annotation { "Feature Type Name" : "Feature", "Feature Type Description" : "" }
export const myFeature = defineFeature(function(context is Context, id is Id, definition is map)
    precondition{}
    {
        {
            var Q0;
            Q0=qCreatedBy(makeId("Front.planeOp"),FACE);
            var sketch = newSketch(context, id + "F0", { "sketchPlane" : qUnion([Q0])});
            skLineSegment(sketch, "E0", {"start": v(0, 22.3) * mm, "end": v(0, 0) * mm, "construction": true});
            skFitSpline(sketch, "E1", {"points": [v(-61.07, -6.98) * mm, v(-58.94, -7.84) * mm, v(-56.34, -8.22) * mm, v(-48.16, -8.6) * mm, v(-38.05, -8.76) * mm, v(-26.12, -8.98) * mm, v(-21.91, -9.15) * mm, v(-14.6, -9.33) * mm, v(-3.24, -9.5) * mm, v(13.49, -9.38) * mm, v(17.24, -9.26) * mm, v(19, -9.14) * mm, v(20.21, -8.9) * mm, v(21.52, -8.48) * mm, v(22.05, -7.83) * mm, v(22.5, -7.27) * mm, v(23.16, -6.84) * mm, v(23.97, -6.5) * mm, v(24.57, -5.86) * mm, v(24.95, -5.03) * mm, v(24.92, -4.13) * mm, v(24.43, -3.44) * mm, v(23.83, -2.92) * mm, v(23.16, -2.63) * mm, v(22.5, -2.17) * mm, v(22.12, -2.03) * mm, v(21.75, -1.57) * mm, v(21.09, -1.13) * mm, v(20.4, -0.79) * mm, v(19.33, -0.56) * mm, v(17.83, -0.36) * mm, v(16.39, -0.24) * mm, v(14.53, -0.14) * mm, v(12.17, -0.05) * mm, v(10.07, 0) * mm], "startDerivative": vector(72.66, -33.25) * mm, "endDerivative": vector(-73.02, 1.43) * mm});
            skArc(sketch, "E2", {"start": v(18.34, 2.78) * mm, "mid": v(14.1, 1.7) * mm, "end": v(10.07, 0) * mm});
            skLineSegment(sketch, "E3", {"start": v(-61.07, -6.98) * mm, "end": v(-61.07, -2.65) * mm});
            skArc(sketch, "E4", {"start": v(18.34, 2.78) * mm, "mid": v(20.82, 2.08) * mm, "end": v(23.39, 1.8) * mm});
            skArc(sketch, "E5", {"start": v(23.39, 1.8) * mm, "mid": v(26.49, 1.03) * mm, "end": v(29.58, 1.8) * mm});
            skArc(sketch, "E6", {"start": v(29.58, 1.8) * mm, "mid": v(32.23, 2.03) * mm, "end": v(34.77, 2.78) * mm});
            skLineSegment(sketch, "E7", {"start": v(34.77, 2.78) * mm, "end": v(61.14, 3.32) * mm});
            skLineSegment(sketch, "E8", {"start": v(61.14, 3.32) * mm, "end": v(62.06, 5.86) * mm});
            skLineSegment(sketch, "E9", {"start": v(62.06, 5.86) * mm, "end": v(47.49, 5.86) * mm});
            skLineSegment(sketch, "E10", {"start": v(47.49, 5.86) * mm, "end": v(47.03, 6.17) * mm});
            skLineSegment(sketch, "E11", {"start": v(47.03, 6.17) * mm, "end": v(43.68, 6.17) * mm});
            skArc(sketch, "E12", {"start": v(35.62, 7.65) * mm, "mid": v(39.58, 6.54) * mm, "end": v(43.68, 6.17) * mm});
            skLineSegment(sketch, "E13", {"start": v(35.62, 7.65) * mm, "end": v(34.47, 8.77) * mm});
            skLineSegment(sketch, "E14", {"start": v(34.47, 8.77) * mm, "end": v(30.37, 8.77) * mm});
            skLineSegment(sketch, "E15", {"start": v(30.37, 8.77) * mm, "end": v(29.74, 9.25) * mm});
            skLineSegment(sketch, "E16", {"start": v(29.74, 9.25) * mm, "end": v(29.74, 9.51) * mm});
            skArc(sketch, "E17", {"start": v(29.74, 9.51) * mm, "mid": v(29.04, 9.84) * mm, "end": v(28.29, 9.97) * mm});
            skLineSegment(sketch, "E18", {"start": v(28.29, 9.97) * mm, "end": v(27.74, 9.97) * mm});
            skArc(sketch, "E19", {"start": v(27.74, 9.97) * mm, "mid": v(26.66, 10.33) * mm, "end": v(25.58, 9.97) * mm});
            skLineSegment(sketch, "E20", {"start": v(25.58, 9.97) * mm, "end": v(22.22, 9.85) * mm});
            skArc(sketch, "E21", {"start": v(22.22, 9.85) * mm, "mid": v(21.65, 9.7) * mm, "end": v(21.2, 9.32) * mm});
            skLineSegment(sketch, "E22", {"start": v(21.2, 9.32) * mm, "end": v(0.14, 10) * mm});
            skLineSegment(sketch, "E23", {"start": v(0.14, 10) * mm, "end": v(-2.32, 11.15) * mm});
            skPoint(sketch, "E23.endSnap0", {"position": v(0, 11.15) * mm});
            skArc(sketch, "E24", {"start": v(-2.32, 11.15) * mm, "mid": v(-0.13, 11.24) * mm, "end": v(2.04, 11.57) * mm});
            skArc(sketch, "E25", {"start": v(2.04, 11.57) * mm, "mid": v(3, 11.9) * mm, "end": v(3.7, 12.63) * mm});
            skLineSegment(sketch, "E26", {"start": v(3.7, 12.63) * mm, "end": v(3.7, 13.61) * mm});
            skLineSegment(sketch, "E27", {"start": v(3.7, 13.61) * mm, "end": v(5.25, 13.61) * mm});
            skArc(sketch, "E28", {"start": v(5.25, 13.61) * mm, "mid": v(5.55, 12.74) * mm, "end": v(6.1, 12.02) * mm});
            skLineSegment(sketch, "E29", {"start": v(6.1, 12.02) * mm, "end": v(6.52, 12.02) * mm});
            skLineSegment(sketch, "E30", {"start": v(6.52, 12.02) * mm, "end": v(6.52, 18.6) * mm});
            skLineSegment(sketch, "E31", {"start": v(6.52, 18.6) * mm, "end": v(6.1, 18.6) * mm});
            skArc(sketch, "E32", {"start": v(6.1, 18.6) * mm, "mid": v(5.55, 17.74) * mm, "end": v(5.25, 16.77) * mm});
            skLineSegment(sketch, "E33", {"start": v(5.25, 16.77) * mm, "end": v(3.79, 16.77) * mm});
            skLineSegment(sketch, "E34", {"start": v(3.79, 16.77) * mm, "end": v(3.79, 17.93) * mm});
            skArc(sketch, "E35", {"start": v(3.79, 17.93) * mm, "mid": v(2.94, 18.66) * mm, "end": v(1.86, 18.94) * mm});
            skLineSegment(sketch, "E36", {"start": v(1.86, 18.94) * mm, "end": v(-0.16, 19.06) * mm});
            skArc(sketch, "E37", {"start": v(-0.16, 19.06) * mm, "mid": v(-0.64, 19.4) * mm, "end": v(-1.22, 19.53) * mm});
            skFitSpline(sketch, "E38", {"points": [v(-1.22, 19.53) * mm, v(-2.68, 19.64) * mm, v(-5.39, 19.67) * mm, v(-7.1, 19.65) * mm, v(-13.35, 19.67) * mm, v(-26.7, 19.24) * mm, v(-37.9, 18.34) * mm], "startDerivative": vector(-14.6, 1.5) * mm, "endDerivative": vector(-43.75, -4.05) * mm});
            skFitSpline(sketch, "E39", {"points": [v(-37.9, 18.34) * mm, v(-38.41, 17.33) * mm, v(-39.6, 16.45) * mm, v(-41.1, 15.84) * mm, v(-42.02, 15.63) * mm], "startDerivative": vector(-1.75, -4.5) * mm, "endDerivative": vector(-4, -0.72) * mm});
            skLineSegment(sketch, "E40", {"start": v(-42.02, 15.63) * mm, "end": v(-42.02, 13.4) * mm});
            skFitSpline(sketch, "E41", {"points": [v(-42.02, 13.4) * mm, v(-39.98, 13.28) * mm, v(-37.97, 13.08) * mm, v(-36.61, 12.92) * mm], "startDerivative": vector(5.67, -0.24) * mm, "endDerivative": vector(4.42, -0.52) * mm});
            skFitSpline(sketch, "E42", {"points": [v(-36.61, 12.92) * mm, v(-36.14, 12.41) * mm, v(-35.35, 11.98) * mm], "startDerivative": vector(0.9, -1.15) * mm, "endDerivative": vector(1.6, -0.75) * mm});
            skFitSpline(sketch, "E43", {"points": [v(-35.35, 11.98) * mm, v(-30.42, 11.58) * mm, v(-24.46, 11.34) * mm, v(-19.95, 11.19) * mm, v(-17.23, 11.19) * mm], "startDerivative": vector(18.11, -1.69) * mm, "endDerivative": vector(13.15, 0.13) * mm});
            skLineSegment(sketch, "E44", {"start": v(-17.23, 11.19) * mm, "end": v(-10.45, 8.48) * mm});
            skLineSegment(sketch, "E45", {"start": v(-10.45, 8.48) * mm, "end": v(-8.63, 6.53) * mm});
            skLineSegment(sketch, "E46", {"start": v(-8.63, 6.53) * mm, "end": v(-10.68, 5.14) * mm});
            skLineSegment(sketch, "E47", {"start": v(-10.68, 5.14) * mm, "end": v(-8.18, 3.37) * mm});
            skLineSegment(sketch, "E48", {"start": v(-8.18, 3.37) * mm, "end": v(-4.86, 3.37) * mm});
            skLineSegment(sketch, "E49", {"start": v(-4.86, 3.37) * mm, "end": v(-5.27, 2.44) * mm});
            skLineSegment(sketch, "E50", {"start": v(-5.27, 2.44) * mm, "end": v(-13.89, 0) * mm});
            skFitSpline(sketch, "E51", {"points": [v(-61.07, -2.65) * mm, v(-60.98, -2.39) * mm, v(-60.7, -2.23) * mm, v(-59.8, -2.03) * mm, v(-58.51, -1.75) * mm, v(-57.1, -1.48) * mm, v(-56.48, -1.4) * mm, v(-55.65, -1.24) * mm, v(-46.62, -0.9) * mm, v(-37.29, -0.61) * mm, v(-28, -0.37) * mm, v(-13.89, 0) * mm], "startDerivative": vector(1.99, 10.5) * mm, "endDerivative": vector(74.9, 2) * mm});
            skSolve(sketch);
        }
        {
            var Q0;
            Q0 = qSketchRegion(id + "F0", true);
            extrude(context, id + "F1", {"entities" : qUnion([Q0]), "depth" : 2 * mm, "offsetDistance" : 25 * mm});
        }
        {
            var Q0;
            Q0=makeQuery(id+"F1.opExtrude","SWEPT_BODY",BODY,{"disambiguationData":[OSD([sQuery(id+"F0.wireOp",EDGE,"E1"),sQuery(id+"F0.wireOp",EDGE,"E2"),sQuery(id+"F0.wireOp",EDGE,"E3"),sQuery(id+"F0.wireOp",EDGE,"E4"),sQuery(id+"F0.wireOp",EDGE,"E5"),sQuery(id+"F0.wireOp",EDGE,"E6"),sQuery(id+"F0.wireOp",EDGE,"E7"),sQuery(id+"F0.wireOp",EDGE,"E8"),sQuery(id+"F0.wireOp",EDGE,"E9"),sQuery(id+"F0.wireOp",EDGE,"E10"),sQuery(id+"F0.wireOp",EDGE,"E11"),sQuery(id+"F0.wireOp",EDGE,"E12"),sQuery(id+"F0.wireOp",EDGE,"E13"),sQuery(id+"F0.wireOp",EDGE,"E14"),sQuery(id+"F0.wireOp",EDGE,"E15"),sQuery(id+"F0.wireOp",EDGE,"E16"),sQuery(id+"F0.wireOp",EDGE,"E17"),sQuery(id+"F0.wireOp",EDGE,"E18"),sQuery(id+"F0.wireOp",EDGE,"E19"),sQuery(id+"F0.wireOp",EDGE,"E20"),sQuery(id+"F0.wireOp",EDGE,"E21"),sQuery(id+"F0.wireOp",EDGE,"E22"),sQuery(id+"F0.wireOp",EDGE,"E23"),sQuery(id+"F0.wireOp",EDGE,"E24"),sQuery(id+"F0.wireOp",EDGE,"E25"),sQuery(id+"F0.wireOp",EDGE,"E26"),sQuery(id+"F0.wireOp",EDGE,"E27"),sQuery(id+"F0.wireOp",EDGE,"E28"),sQuery(id+"F0.wireOp",EDGE,"E29"),sQuery(id+"F0.wireOp",EDGE,"E30"),sQuery(id+"F0.wireOp",EDGE,"E31"),sQuery(id+"F0.wireOp",EDGE,"E32"),sQuery(id+"F0.wireOp",EDGE,"E33"),sQuery(id+"F0.wireOp",EDGE,"E34"),sQuery(id+"F0.wireOp",EDGE,"E35"),sQuery(id+"F0.wireOp",EDGE,"E36"),sQuery(id+"F0.wireOp",EDGE,"E37"),sQuery(id+"F0.wireOp",EDGE,"E38"),sQuery(id+"F0.wireOp",EDGE,"E39"),sQuery(id+"F0.wireOp",EDGE,"E40"),sQuery(id+"F0.wireOp",EDGE,"E41"),sQuery(id+"F0.wireOp",EDGE,"E42"),sQuery(id+"F0.wireOp",EDGE,"E43"),sQuery(id+"F0.wireOp",EDGE,"E44"),sQuery(id+"F0.wireOp",EDGE,"E45"),sQuery(id+"F0.wireOp",EDGE,"E46"),sQuery(id+"F0.wireOp",EDGE,"E47"),sQuery(id+"F0.wireOp",EDGE,"E48"),sQuery(id+"F0.wireOp",EDGE,"E49"),sQuery(id+"F0.wireOp",EDGE,"E50"),sQuery(id+"F0.wireOp",EDGE,"E51")])]});
            var Q1;
            Q1=makeQuery(id+"F1.opExtrude","CAP_EDGE",EDGE,{"disambiguationData":[OSD([sQuery(id+"F0.wireOp",EDGE,"E3")])],"isStart":false});
            var Q2;
            Q2=makeQuery(id+"F1.opExtrude","CAP_VERTEX",VERTEX,{"disambiguationData":[OSD([sQuery(id+"F0.wireOp",EDGE,"E1"),sQuery(id+"F0.wireOp",EDGE,"E3")])],"isStart":false});
            transform(context, id + "F2", {"entities" : qUnion([Q0]), "transformType" : TransformType.SCALE_UNIFORMLY, "scale" : 1.22, "scalePoint" : qUnion([Q2]), "makeCopy" : false});
        }
        {
            var Q0;
            Q0=makeQuery(id+"F1.opExtrude","CAP_FACE",FACE,{"disambiguationData":[OSD([sQuery(id+"F0.wireOp",EDGE,"E1"),sQuery(id+"F0.wireOp",EDGE,"E2"),sQuery(id+"F0.wireOp",EDGE,"E3"),sQuery(id+"F0.wireOp",EDGE,"E4"),sQuery(id+"F0.wireOp",EDGE,"E5"),sQuery(id+"F0.wireOp",EDGE,"E6"),sQuery(id+"F0.wireOp",EDGE,"E7"),sQuery(id+"F0.wireOp",EDGE,"E8"),sQuery(id+"F0.wireOp",EDGE,"E9"),sQuery(id+"F0.wireOp",EDGE,"E10"),sQuery(id+"F0.wireOp",EDGE,"E11"),sQuery(id+"F0.wireOp",EDGE,"E12"),sQuery(id+"F0.wireOp",EDGE,"E13"),sQuery(id+"F0.wireOp",EDGE,"E14"),sQuery(id+"F0.wireOp",EDGE,"E15"),sQuery(id+"F0.wireOp",EDGE,"E16"),sQuery(id+"F0.wireOp",EDGE,"E17"),sQuery(id+"F0.wireOp",EDGE,"E18"),sQuery(id+"F0.wireOp",EDGE,"E19"),sQuery(id+"F0.wireOp",EDGE,"E20"),sQuery(id+"F0.wireOp",EDGE,"E21"),sQuery(id+"F0.wireOp",EDGE,"E22"),sQuery(id+"F0.wireOp",EDGE,"E23"),sQuery(id+"F0.wireOp",EDGE,"E24"),sQuery(id+"F0.wireOp",EDGE,"E25"),sQuery(id+"F0.wireOp",EDGE,"E26"),sQuery(id+"F0.wireOp",EDGE,"E27"),sQuery(id+"F0.wireOp",EDGE,"E28"),sQuery(id+"F0.wireOp",EDGE,"E29"),sQuery(id+"F0.wireOp",EDGE,"E30"),sQuery(id+"F0.wireOp",EDGE,"E31"),sQuery(id+"F0.wireOp",EDGE,"E32"),sQuery(id+"F0.wireOp",EDGE,"E33"),sQuery(id+"F0.wireOp",EDGE,"E34"),sQuery(id+"F0.wireOp",EDGE,"E35"),sQuery(id+"F0.wireOp",EDGE,"E36"),sQuery(id+"F0.wireOp",EDGE,"E37"),sQuery(id+"F0.wireOp",EDGE,"E38"),sQuery(id+"F0.wireOp",EDGE,"E39"),sQuery(id+"F0.wireOp",EDGE,"E40"),sQuery(id+"F0.wireOp",EDGE,"E41"),sQuery(id+"F0.wireOp",EDGE,"E42"),sQuery(id+"F0.wireOp",EDGE,"E43"),sQuery(id+"F0.wireOp",EDGE,"E44"),sQuery(id+"F0.wireOp",EDGE,"E45"),sQuery(id+"F0.wireOp",EDGE,"E46"),sQuery(id+"F0.wireOp",EDGE,"E47"),sQuery(id+"F0.wireOp",EDGE,"E48"),sQuery(id+"F0.wireOp",EDGE,"E49"),sQuery(id+"F0.wireOp",EDGE,"E50"),sQuery(id+"F0.wireOp",EDGE,"E51")])],"isStart":false});
            var sketch = newSketch(context, id + "F3", { "sketchPlane" : qUnion([Q0])});
            skLineSegment(sketch, "E52.bottom", {"start": v(-8.5, -6) * mm, "end": v(8.5, -6) * mm});
            skLineSegment(sketch, "E52.top", {"start": v(-8.5, -16) * mm, "end": v(8.5, -16) * mm});
            skLineSegment(sketch, "E52.left", {"start": v(-8.5, -6) * mm, "end": v(-8.5, -16) * mm});
            skLineSegment(sketch, "E52.right", {"start": v(8.5, -6) * mm, "end": v(8.5, -16) * mm});
            skLineSegment(sketch, "E53", {"start": v(0, 0) * mm, "end": v(0, -6) * mm, "construction": true});
            skLineSegment(sketch, "E54", {"start": v(-8.5, -16) * mm, "end": v(-44.41, -16) * mm});
            skLineSegment(sketch, "E55", {"start": v(-44.41, -16) * mm, "end": v(-54.41, -21.77) * mm});
            skLineSegment(sketch, "E56", {"start": v(-54.41, -21.77) * mm, "end": v(-54.41, -34) * mm});
            skLineSegment(sketch, "E57.MirrorCS", {"start": v(44.41, -16) * mm, "end": v(54.41, -21.77) * mm});
            skLineSegment(sketch, "E58.MirrorCS", {"start": v(8.5, -16) * mm, "end": v(44.41, -16) * mm});
            skLineSegment(sketch, "E59.MirrorCS", {"start": v(54.41, -21.77) * mm, "end": v(54.41, -34) * mm});
            skLineSegment(sketch, "E60", {"start": v(-54.41, -34) * mm, "end": v(54.41, -34) * mm});
            skText(sketch, "E61", { "text": "USS KELVIN", "fontName": "OpenSans-Bold.ttf"});
            skLineSegment(sketch, "E62", {"start": v(-44.41, -34) * mm, "end": v(-24.2, -69) * mm});
            skLineSegment(sketch, "E63", {"start": v(-24.2, -69) * mm, "end": v(24.2, -69) * mm});
            skLineSegment(sketch, "E64", {"start": v(24.2, -69) * mm, "end": v(44.41, -34) * mm});
            skLineSegment(sketch, "E65", {"start": v(0, -30) * mm, "end": v(0, -69) * mm, "construction": true});
            skLineSegment(sketch, "E66.0", {"start": v(18.43, -59) * mm, "end": v(32.86, -34) * mm});
            skLineSegment(sketch, "E66.1", {"start": v(-18.43, -59) * mm, "end": v(18.43, -59) * mm});
            skLineSegment(sketch, "E66.2", {"start": v(-32.86, -34) * mm, "end": v(-18.43, -59) * mm});
            const initialGuessF3  = {"E61": [-0.03941, -0.03, 1, 0, 0.01]};
            skSetInitialGuess(sketch, initialGuessF3);
            skSolve(sketch);
        }
        {
            var Q0;
            Q0 = qSketchRegion(id + "F3", true);
            var Q1;
            Q1=makeQuery(id+"F1.opExtrude","CAP_FACE",FACE,{"disambiguationData":[OSD([sQuery(id+"F0.wireOp",EDGE,"E1"),sQuery(id+"F0.wireOp",EDGE,"E2"),sQuery(id+"F0.wireOp",EDGE,"E3"),sQuery(id+"F0.wireOp",EDGE,"E4"),sQuery(id+"F0.wireOp",EDGE,"E5"),sQuery(id+"F0.wireOp",EDGE,"E6"),sQuery(id+"F0.wireOp",EDGE,"E7"),sQuery(id+"F0.wireOp",EDGE,"E8"),sQuery(id+"F0.wireOp",EDGE,"E9"),sQuery(id+"F0.wireOp",EDGE,"E10"),sQuery(id+"F0.wireOp",EDGE,"E11"),sQuery(id+"F0.wireOp",EDGE,"E12"),sQuery(id+"F0.wireOp",EDGE,"E13"),sQuery(id+"F0.wireOp",EDGE,"E14"),sQuery(id+"F0.wireOp",EDGE,"E15"),sQuery(id+"F0.wireOp",EDGE,"E16"),sQuery(id+"F0.wireOp",EDGE,"E17"),sQuery(id+"F0.wireOp",EDGE,"E18"),sQuery(id+"F0.wireOp",EDGE,"E19"),sQuery(id+"F0.wireOp",EDGE,"E20"),sQuery(id+"F0.wireOp",EDGE,"E21"),sQuery(id+"F0.wireOp",EDGE,"E22"),sQuery(id+"F0.wireOp",EDGE,"E23"),sQuery(id+"F0.wireOp",EDGE,"E24"),sQuery(id+"F0.wireOp",EDGE,"E25"),sQuery(id+"F0.wireOp",EDGE,"E26"),sQuery(id+"F0.wireOp",EDGE,"E27"),sQuery(id+"F0.wireOp",EDGE,"E28"),sQuery(id+"F0.wireOp",EDGE,"E29"),sQuery(id+"F0.wireOp",EDGE,"E30"),sQuery(id+"F0.wireOp",EDGE,"E31"),sQuery(id+"F0.wireOp",EDGE,"E32"),sQuery(id+"F0.wireOp",EDGE,"E33"),sQuery(id+"F0.wireOp",EDGE,"E34"),sQuery(id+"F0.wireOp",EDGE,"E35"),sQuery(id+"F0.wireOp",EDGE,"E36"),sQuery(id+"F0.wireOp",EDGE,"E37"),sQuery(id+"F0.wireOp",EDGE,"E38"),sQuery(id+"F0.wireOp",EDGE,"E39"),sQuery(id+"F0.wireOp",EDGE,"E40"),sQuery(id+"F0.wireOp",EDGE,"E41"),sQuery(id+"F0.wireOp",EDGE,"E42"),sQuery(id+"F0.wireOp",EDGE,"E43"),sQuery(id+"F0.wireOp",EDGE,"E44"),sQuery(id+"F0.wireOp",EDGE,"E45"),sQuery(id+"F0.wireOp",EDGE,"E46"),sQuery(id+"F0.wireOp",EDGE,"E47"),sQuery(id+"F0.wireOp",EDGE,"E48"),sQuery(id+"F0.wireOp",EDGE,"E49"),sQuery(id+"F0.wireOp",EDGE,"E50"),sQuery(id+"F0.wireOp",EDGE,"E51")])],"isStart":true});
            extrude(context, id + "F4", {"entities" : qUnion([Q0]), "operationType" : NewBodyOperationType.ADD, "endBound" : BoundingType.UP_TO_SURFACE, "oppositeDirection" : true, "depth" : 25 * mm, "endBoundEntityFace" : qUnion([Q1]), "offsetDistance" : 25 * mm});
        }
        {
            var Q0;
            Q0=makeQuery(id+"F4.opExtrude","SWEPT_EDGE",EDGE,{"disambiguationData":[OSD([sQuery(id+"F3.wireOp",EDGE,"E66.1"),sQuery(id+"F3.wireOp",EDGE,"E66.2")])]});
            var Q1;
            Q1=makeQuery(id+"F4.opExtrude","SWEPT_EDGE",EDGE,{"disambiguationData":[OSD([sQuery(id+"F3.wireOp",EDGE,"E66.0"),sQuery(id+"F3.wireOp",EDGE,"E66.1")])]});
            var Q2;
            Q2=makeQuery(id+"F4.opExtrude","SWEPT_EDGE",EDGE,{"disambiguationData":[OSD([sQuery(id+"F3.wireOp",EDGE,"E55"),sQuery(id+"F3.wireOp",EDGE,"E56")])]});
            var Q3;
            Q3=makeQuery(id+"F4.opExtrude","SWEPT_EDGE",EDGE,{"disambiguationData":[OSD([sQuery(id+"F3.wireOp",EDGE,"E54"),sQuery(id+"F3.wireOp",EDGE,"E55")])]});
            var Q4;
            Q4=makeQuery(id+"F4.opExtrude","SWEPT_EDGE",EDGE,{"disambiguationData":[OSD([sQuery(id+"F3.wireOp",EDGE,"E56"),sQuery(id+"F3.wireOp",EDGE,"E60")])]});
            var Q5;
            Q5=makeQuery(id+"F4.opExtrude","SWEPT_EDGE",EDGE,{"disambiguationData":[OSD([sQuery(id+"F3.wireOp",EDGE,"E57.MirrorCS"),sQuery(id+"F3.wireOp",EDGE,"E58.MirrorCS")])]});
            var Q6;
            Q6=makeQuery(id+"F4.opExtrude","SWEPT_EDGE",EDGE,{"disambiguationData":[OSD([sQuery(id+"F3.wireOp",EDGE,"E57.MirrorCS"),sQuery(id+"F3.wireOp",EDGE,"E59.MirrorCS")])]});
            var Q7;
            Q7=makeQuery(id+"F4.opExtrude","SWEPT_EDGE",EDGE,{"disambiguationData":[OSD([sQuery(id+"F3.wireOp",EDGE,"E59.MirrorCS"),sQuery(id+"F3.wireOp",EDGE,"E60")])]});
            fillet(context, id + "F5", {"entities" : qUnion([Q0, Q1, Q2, Q3, Q4, Q5, Q6, Q7]), "radius" : 5 * mm, "tangentPropagation" : true, "allowEdgeOverflow" : false});
        }
        {
            var Q0;
            Q0=makeQuery(id+"F4.opExtrude","SWEPT_EDGE",EDGE,{"disambiguationData":[OSD([sQuery(id+"F3.wireOp",EDGE,"E62"),sQuery(id+"F3.wireOp",EDGE,"E63")])]});
            var Q1;
            Q1=makeQuery(id+"F4.opExtrude","SWEPT_EDGE",EDGE,{"disambiguationData":[OSD([sQuery(id+"F3.wireOp",EDGE,"E63"),sQuery(id+"F3.wireOp",EDGE,"E64")])]});
            fillet(context, id + "F6", {"entities" : qUnion([Q0, Q1]), "radius" : 15 * mm, "tangentPropagation" : true, "allowEdgeOverflow" : false});
        }
        {
            var Q0;
            Q0=qCreatedBy(makeId("Right.planeOp"),FACE);
            var sketch = newSketch(context, id + "F7", { "sketchPlane" : qUnion([Q0])});
            skLineSegment(sketch, "E67.bottom", {"start": v(-4, 27.36) * mm, "end": v(-1.56, 27.36) * mm});
            skLineSegment(sketch, "E67.top", {"start": v(-4, -71) * mm, "end": v(-1.56, -71) * mm});
            skLineSegment(sketch, "E67.left", {"start": v(-4, 27.36) * mm, "end": v(-4, -71) * mm});
            skLineSegment(sketch, "E67.right", {"start": v(-1.56, 27.36) * mm, "end": v(-1.56, -71) * mm});
            skSolve(sketch);
        }
        {
            var Q0;
            Q0 = qSketchRegion(id + "F7", true);
            extrude(context, id + "F8", {"entities" : qUnion([Q0]), "operationType" : NewBodyOperationType.REMOVE, "endBound" : BoundingType.THROUGH_ALL, "oppositeDirection" : true, "depth" : 25 * mm, "offsetDistance" : 25 * mm, "hasSecondDirection" : true, "secondDirectionBound" : SecondDirectionBoundingType.THROUGH_ALL, "secondDirectionOppositeDirection" : false, "secondDirectionDepth" : 25 * mm});
        }
    });